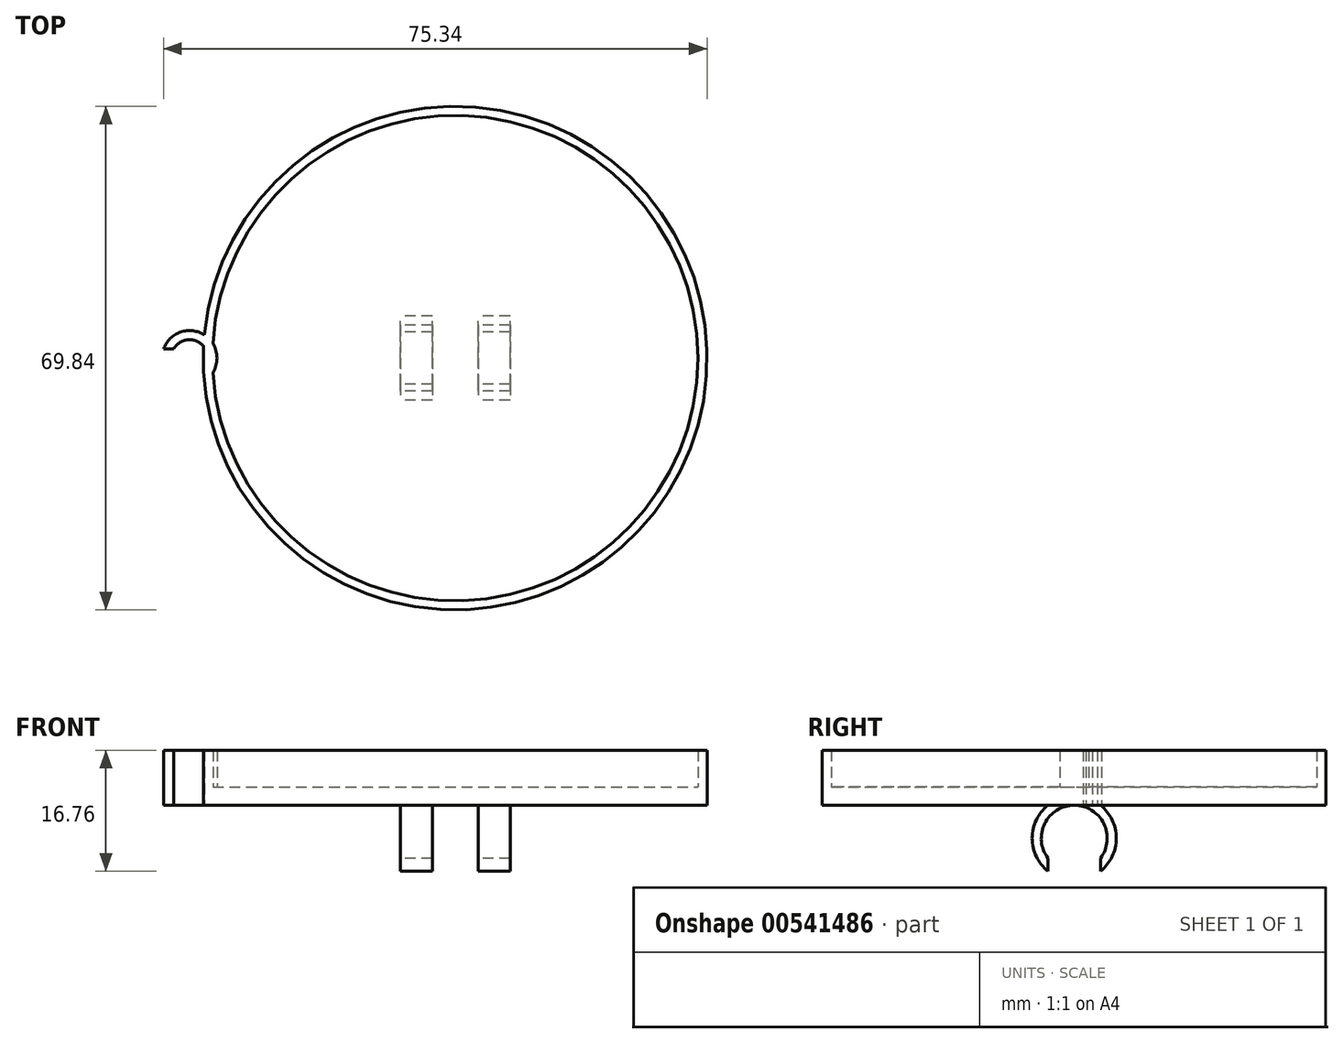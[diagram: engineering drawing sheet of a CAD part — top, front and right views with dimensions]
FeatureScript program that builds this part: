
annotation { "Feature Type Name" : "Feature", "Feature Type Description" : "" }
export const myFeature = defineFeature(function(context is Context, id is Id, definition is map)
    precondition{}
    {
        {
            var Q0;
            Q0=qCreatedBy(makeId("Top.planeOp"),FACE);
            var sketch = newSketch(context, id + "F0", { "sketchPlane" : qUnion([Q0])});
            skCircle(sketch, "E0", {"center": v(0, 0) * mm, "radius": 33.66 * mm});
            skCircle(sketch, "E1", {"center": v(0, 0) * mm, "radius": 34.93 * mm});
            skSolve(sketch);
        }
        {
            var Q0;
            Q0=makeQuery(id+"F0.imprint","IMPRINT",FACE,{"disambiguationData":[TD([[makeQuery(id+"F0.imprint","IMPRINT",EDGE,{"derivedFrom":sQuery(id+"F0.wireOp",EDGE,"E0")}),-1.0]])]});
            extrude(context, id + "F1", {"entities" : qUnion([Q0]), "depth" : 7.62 * mm, "offsetDistance" : 25.4 * mm});
        }
        {
            var Q0;
            Q0=makeQuery(id+"F0.imprint","IMPRINT",FACE,{"disambiguationData":[TD([[makeQuery(id+"F0.imprint","IMPRINT",EDGE,{"derivedFrom":sQuery(id+"F0.wireOp",EDGE,"E0")}),1.0]])]});
            extrude(context, id + "F2", {"entities" : qUnion([Q0]), "operationType" : NewBodyOperationType.ADD, "depth" : 2.54 * mm, "offsetDistance" : 25.4 * mm});
        }
        {
            var Q0;
            Q0=qCreatedBy(makeId("Right.planeOp"),FACE);
            var sketch = newSketch(context, id + "F3", { "sketchPlane" : qUnion([Q0])});
            skCircle(sketch, "E2", {"center": v(0, -4.57) * mm, "radius": 4.57 * mm});
            skCircle(sketch, "E3", {"center": v(0, -4.57) * mm, "radius": 5.84 * mm});
            skSolve(sketch);
        }
        {
            var Q0;
            Q0=makeQuery(id+"F3.imprint","IMPRINT",FACE,{"disambiguationData":[TD([[makeQuery(id+"F3.imprint","IMPRINT",EDGE,{"derivedFrom":sQuery(id+"F3.wireOp",EDGE,"E2")}),-1.0]])]});
            extrude(context, id + "F4", {"entities" : qUnion([Q0]), "operationType" : NewBodyOperationType.ADD, "depth" : 7.62 * mm, "offsetDistance" : 25.4 * mm, "hasSecondDirection" : true, "secondDirectionOppositeDirection" : true, "secondDirectionDepth" : 7.62 * mm});
        }
        {
            var Q0;
            {var subQ0=sQuery(id+"F0.wireOp",EDGE,"E0");Q0=makeQuery(id+"F2.boolean.opBoolean","MERGE",FACE,{"derivedFrom":[makeQuery(id+"F1.opExtrude","CAP_FACE",FACE,{"disambiguationData":[OSD([subQ0,sQuery(id+"F0.wireOp",EDGE,"E1")])],"isStart":true}),makeQuery(id+"F2.opExtrude","CAP_FACE",FACE,{"disambiguationData":[OSD([subQ0])],"isStart":true})]});}
            var sketch = newSketch(context, id + "F5", { "sketchPlane" : qUnion([Q0])});
            skLineSegment(sketch, "E4.bottom", {"start": v(-14.7, 3.81) * mm, "end": v(13.92, 3.81) * mm});
            skLineSegment(sketch, "E4.top", {"start": v(-14.7, -3.81) * mm, "end": v(13.92, -3.81) * mm});
            skLineSegment(sketch, "E4.left", {"start": v(-14.7, 3.81) * mm, "end": v(-14.7, -3.81) * mm});
            skLineSegment(sketch, "E4.right", {"start": v(13.92, 3.81) * mm, "end": v(13.92, -3.81) * mm});
            skSolve(sketch);
        }
        {
            var Q0;
            {var subQ0=sQuery(id+"F3.wireOp",EDGE,"E3");var subQ3=sQuery(id+"F0.wireOp",EDGE,"E0");var subQ4=makeQuery(id+"F2.boolean.opBoolean","MERGE",FACE,{"derivedFrom":[makeQuery(id+"F1.opExtrude","CAP_FACE",FACE,{"disambiguationData":[OSD([subQ3,sQuery(id+"F0.wireOp",EDGE,"E1")])],"isStart":true}),makeQuery(id+"F2.opExtrude","CAP_FACE",FACE,{"disambiguationData":[OSD([subQ3])],"isStart":true})]});var subQ6=makeQuery(id+"F4.opExtrude","SWEPT_FACE",FACE,{"disambiguationData":[OSD([subQ0])]});Q0=makeQuery(id+"F5.imprint","IMPRINT",FACE,{"disambiguationData":[TD([[makeQuery(id+"F5.imprint","IMPRINT",EDGE,{"derivedFrom":makeQuery(id+"F4.boolean.opBoolean","INTERSECT",EDGE,{"disambiguationData":[OD(0.0)],"derivedFrom":[subQ4,subQ6]})}),1.0]])]});}
            extrude(context, id + "F6", {"entities" : qUnion([Q0]), "operationType" : NewBodyOperationType.REMOVE, "depth" : 25.4 * mm, "offsetDistance" : 25.4 * mm, "hasSecondDirection" : true, "secondDirectionOppositeDirection" : false, "secondDirectionDepth" : 5.08 * mm});
        }
        {
            var Q0;
            {var subQ0=sQuery(id+"F0.wireOp",EDGE,"E0");Q0=makeQuery(id+"F2.boolean.opBoolean","MERGE",FACE,{"derivedFrom":[makeQuery(id+"F1.opExtrude","CAP_FACE",FACE,{"disambiguationData":[OSD([subQ0,sQuery(id+"F0.wireOp",EDGE,"E1")])],"isStart":true}),makeQuery(id+"F2.opExtrude","CAP_FACE",FACE,{"disambiguationData":[OSD([subQ0])],"isStart":true})]});}
            var sketch = newSketch(context, id + "F7", { "sketchPlane" : qUnion([Q0])});
            skLineSegment(sketch, "E5.bottom", {"start": v(-3.17, 11.88) * mm, "end": v(3.18, 11.88) * mm});
            skLineSegment(sketch, "E5.top", {"start": v(-3.17, -11.1) * mm, "end": v(3.18, -11.1) * mm});
            skLineSegment(sketch, "E5.left", {"start": v(-3.17, 11.88) * mm, "end": v(-3.17, -11.1) * mm});
            skLineSegment(sketch, "E5.right", {"start": v(3.18, 11.88) * mm, "end": v(3.18, -11.1) * mm});
            skSolve(sketch);
        }
        {
            var Q0;
            {var subQ0=sQuery(id+"F7.wireOp",EDGE,"E5.top");Q0=makeQuery(id+"F7.imprint","IMPRINT",FACE,{"disambiguationData":[TD([[makeQuery(id+"F7.imprint","IMPRINT",EDGE,{"derivedFrom":subQ0}),1.0]])]});}
            var Q1;
            {var subQ0=sQuery(id+"F7.wireOp",EDGE,"E5.left");var subQ1=makeQuery(id+"F4.opExtrude","SWEPT_FACE",FACE,{"disambiguationData":[OSD([sQuery(id+"F3.wireOp",EDGE,"E3")])]});var subQ2=sQuery(id+"F0.wireOp",EDGE,"E0");var subQ3=makeQuery(id+"F2.boolean.opBoolean","MERGE",FACE,{"derivedFrom":[makeQuery(id+"F1.opExtrude","CAP_FACE",FACE,{"disambiguationData":[OSD([subQ2,sQuery(id+"F0.wireOp",EDGE,"E1")])],"isStart":true}),makeQuery(id+"F2.opExtrude","CAP_FACE",FACE,{"disambiguationData":[OSD([subQ2])],"isStart":true})]});var subQ4=makeQuery(id+"F4.boolean.opBoolean","INTERSECT",EDGE,{"disambiguationData":[OD(0.0)],"derivedFrom":[subQ3,subQ1]});var subQ5=makeQuery(id+"F7.imprint","INTERSECT",VERTEX,{"derivedFrom":[subQ4,subQ0]});Q1=makeQuery(id+"F7.imprint","IMPRINT",FACE,{"disambiguationData":[TD([[makeQuery(id+"F7.imprint","IMPRINT",EDGE,{"disambiguationData":[TD([[subQ5,-1.0]])],"derivedFrom":subQ0}),1.0]])]});}
            var Q2;
            {var subQ0=sQuery(id+"F7.wireOp",EDGE,"E5.bottom");Q2=makeQuery(id+"F7.imprint","IMPRINT",FACE,{"disambiguationData":[TD([[makeQuery(id+"F7.imprint","IMPRINT",EDGE,{"derivedFrom":subQ0}),-1.0]])]});}
            extrude(context, id + "F8", {"entities" : qUnion([Q0, Q1, Q2]), "operationType" : NewBodyOperationType.REMOVE, "depth" : 25.4 * mm, "offsetDistance" : 25.4 * mm});
        }
        {
            var Q0;
            {var subQ0=sQuery(id+"F0.wireOp",EDGE,"E0");Q0=makeQuery(id+"F8.boolean.opBoolean","MERGE",FACE,{"derivedFrom":[makeQuery(id+"F2.boolean.opBoolean","MERGE",FACE,{"derivedFrom":[makeQuery(id+"F1.opExtrude","CAP_FACE",FACE,{"disambiguationData":[OSD([subQ0,sQuery(id+"F0.wireOp",EDGE,"E1")])],"isStart":true}),makeQuery(id+"F2.opExtrude","CAP_FACE",FACE,{"disambiguationData":[OSD([subQ0])],"isStart":true})]}),makeQuery(id+"F8.opExtrude","CAP_FACE",FACE,{"disambiguationData":[OSD([sQuery(id+"F7.wireOp",EDGE,"E5.bottom"),sQuery(id+"F7.wireOp",EDGE,"E5.top"),sQuery(id+"F7.wireOp",EDGE,"E5.left"),sQuery(id+"F7.wireOp",EDGE,"E5.right")])],"isStart":true})]});}
            var sketch = newSketch(context, id + "F9", { "sketchPlane" : qUnion([Q0])});
            skCircle(sketch, "E6", {"center": v(-36.83, 0) * mm, "radius": 3.81 * mm});
            skCircle(sketch, "E7", {"center": v(-36.83, 0) * mm, "radius": 2.54 * mm});
            skLineSegment(sketch, "E8.bottom", {"start": v(-40.77, 1.27) * mm, "end": v(-36.6, 1.27) * mm});
            skLineSegment(sketch, "E8.top", {"start": v(-40.77, -1.27) * mm, "end": v(-36.6, -1.27) * mm});
            skLineSegment(sketch, "E8.left", {"start": v(-40.77, 1.27) * mm, "end": v(-40.77, -1.27) * mm});
            skLineSegment(sketch, "E8.right", {"start": v(-36.6, 1.27) * mm, "end": v(-36.6, -1.27) * mm});
            skSolve(sketch);
        }
        {
            var Q0;
            {var subQ1=makeQuery(id+"F1.opExtrude","CAP_EDGE",EDGE,{"disambiguationData":[OSD([sQuery(id+"F0.wireOp",EDGE,"E1")])],"isStart":true});var subQ4=makeQuery(id+"F9.imprint","IMPRINT",VERTEX,{"derivedFrom":subQ1});Q0=makeQuery(id+"F9.imprint","IMPRINT",FACE,{"disambiguationData":[TD([[makeQuery(id+"F9.imprint","IMPRINT",EDGE,{"disambiguationData":[TD([[subQ4,-1.0]])],"derivedFrom":subQ1}),1.0]])]});}
            var Q1;
            {var subQ0=sQuery(id+"F9.wireOp",EDGE,"E6");var subQ1=makeQuery(id+"F1.opExtrude","CAP_EDGE",EDGE,{"disambiguationData":[OSD([sQuery(id+"F0.wireOp",EDGE,"E1")])],"isStart":true});var subQ2=makeQuery(id+"F9.imprint","INTERSECT",VERTEX,{"disambiguationData":[OD(0.0)],"derivedFrom":[subQ1,subQ0]});Q1=makeQuery(id+"F9.imprint","IMPRINT",FACE,{"disambiguationData":[TD([[makeQuery(id+"F9.imprint","IMPRINT",EDGE,{"disambiguationData":[TD([[subQ2,-1.0]])],"derivedFrom":subQ0}),1.0]])]});}
            var Q2;
            {var subQ0=sQuery(id+"F9.wireOp",EDGE,"E8.top");var subQ1=sQuery(id+"F9.wireOp",EDGE,"E6");var subQ2=makeQuery(id+"F9.imprint","INTERSECT",VERTEX,{"derivedFrom":[subQ1,subQ0]});Q2=makeQuery(id+"F9.imprint","IMPRINT",FACE,{"disambiguationData":[TD([[makeQuery(id+"F9.imprint","IMPRINT",EDGE,{"disambiguationData":[TD([[subQ2,-1.0]])],"derivedFrom":subQ1}),1.0]])]});}
            extrude(context, id + "F10", {"entities" : qUnion([Q0, Q1, Q2]), "operationType" : NewBodyOperationType.ADD, "oppositeDirection" : true, "depth" : 7.62 * mm, "offsetDistance" : 25.4 * mm});
        }
    });
